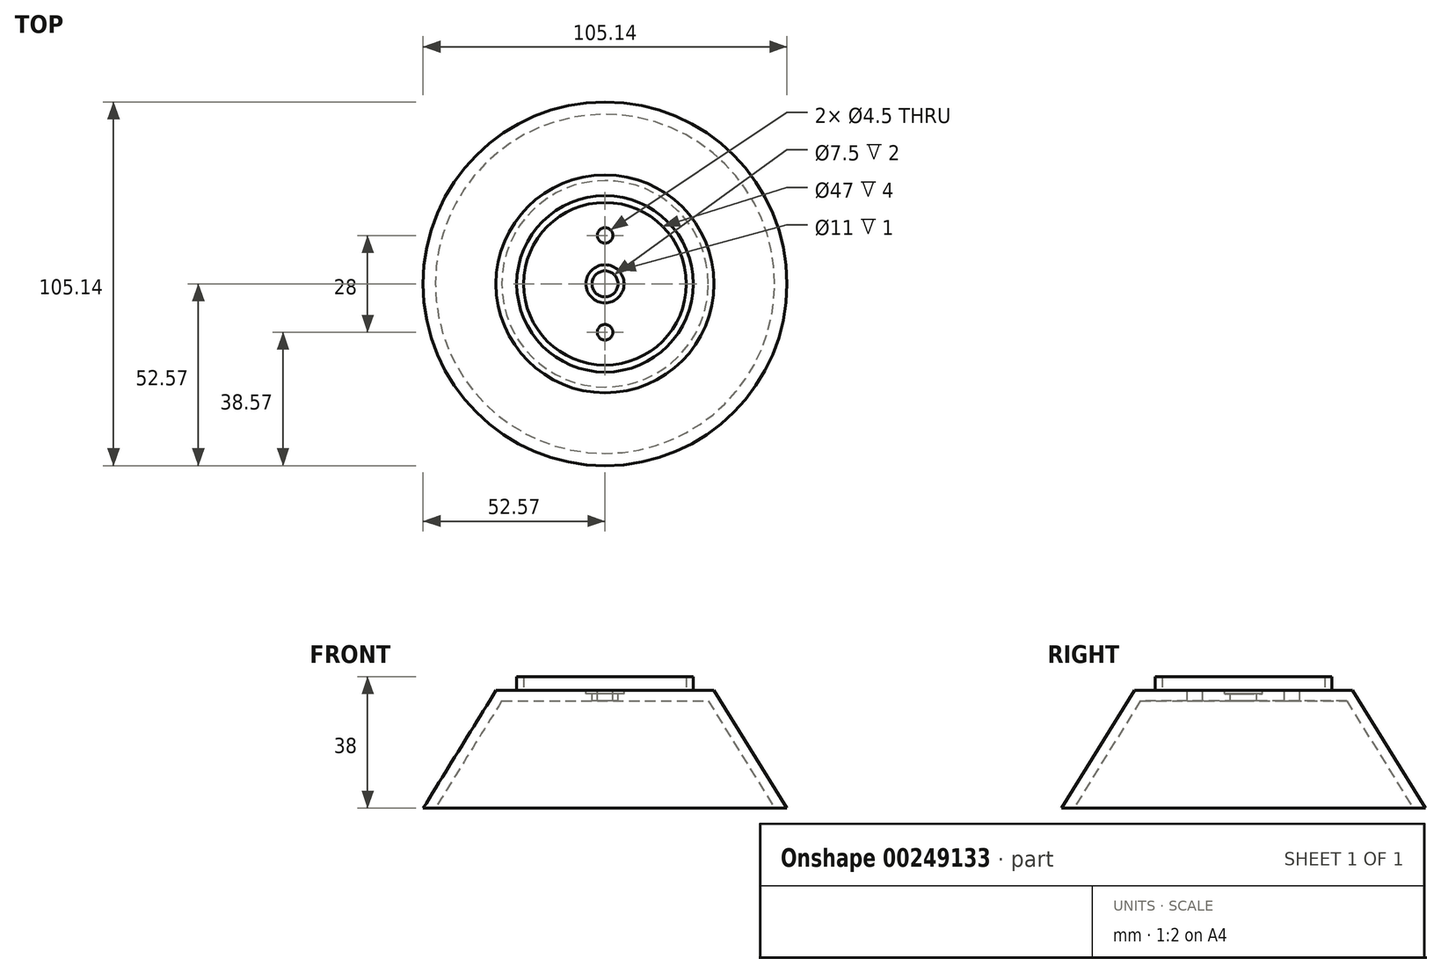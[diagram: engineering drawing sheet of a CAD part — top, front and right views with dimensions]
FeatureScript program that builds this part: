
annotation { "Feature Type Name" : "Feature", "Feature Type Description" : "" }
export const myFeature = defineFeature(function(context is Context, id is Id, definition is map)
    precondition{}
    {
        {
            var Q0;
            Q0=qCreatedBy(makeId("Front.planeOp"),FACE);
            var sketch = newSketch(context, id + "F0", { "sketchPlane" : qUnion([Q0])});
            skLineSegment(sketch, "E0", {"start": v(-23.5, 32.38) * mm, "end": v(-25.5, 32.38) * mm});
            skLineSegment(sketch, "E1", {"start": v(-25.5, 32.38) * mm, "end": v(-25.5, 28.38) * mm});
            skLineSegment(sketch, "E2", {"start": v(-31.5, 28.38) * mm, "end": v(-52.57, -5.62) * mm});
            skLineSegment(sketch, "E3", {"start": v(-49.01, -5.57) * mm, "end": v(-29.83, 25.38) * mm});
            skLineSegment(sketch, "E4", {"start": v(-29.83, 25.38) * mm, "end": v(0, 25.38) * mm});
            skLineSegment(sketch, "E5", {"start": v(0, 25.38) * mm, "end": v(0, 28.38) * mm});
            skLineSegment(sketch, "E6", {"start": v(0, 28.38) * mm, "end": v(-23.5, 28.38) * mm});
            skLineSegment(sketch, "E7", {"start": v(-23.5, 28.38) * mm, "end": v(-23.5, 32.38) * mm});
            skLineSegment(sketch, "E8", {"start": v(-25.5, 28.38) * mm, "end": v(-31.5, 28.38) * mm});
            skLineSegment(sketch, "E9", {"start": v(-52.57, -5.62) * mm, "end": v(-49.01, -5.57) * mm});
            skSolve(sketch);
        }
        {
            var Q0;
            Q0 = qSketchRegion(id + "F0", true);
            var Q1;
            Q1=sQuery(id+"F0.wireOp",EDGE,"E5");
            revolve(context, id + "F1", {"entities" : qUnion([Q0]), "axis" : qUnion([Q1]), "revolveType" : RevolveType.FULL});
        }
        {
            var Q0;
            Q0=makeQuery(id+"F1.opRevolve","SWEPT_FACE",FACE,{"disambiguationData":[OSD([sQuery(id+"F0.wireOp",EDGE,"E6")])]});
            var sketch = newSketch(context, id + "F2", { "sketchPlane" : qUnion([Q0])});
            skCircle(sketch, "E10", {"center": v(0, 0) * mm, "radius": 3.75 * mm});
            skCircle(sketch, "E11", {"center": v(0, -14) * mm, "radius": 2.25 * mm});
            skCircle(sketch, "E12.MirrorC", {"center": v(0, 14) * mm, "radius": 2.25 * mm});
            skSolve(sketch);
        }
        {
            var Q0;
            Q0 = qSketchRegion(id + "F2", true);
            extrude(context, id + "F3", {"entities" : qUnion([Q0]), "operationType" : NewBodyOperationType.REMOVE, "oppositeDirection" : true, "depth" : 25 * mm});
        }
        {
            var Q0;
            Q0=makeQuery(id+"F1.opRevolve","SWEPT_FACE",FACE,{"disambiguationData":[OSD([sQuery(id+"F0.wireOp",EDGE,"E6")])]});
            var sketch = newSketch(context, id + "F4", { "sketchPlane" : qUnion([Q0])});
            skCircle(sketch, "E13", {"center": v(0, 0) * mm, "radius": 5.5 * mm});
            skSolve(sketch);
        }
        {
            var Q0;
            Q0 = qSketchRegion(id + "F4", true);
            extrude(context, id + "F5", {"entities" : qUnion([Q0]), "operationType" : NewBodyOperationType.REMOVE, "oppositeDirection" : true, "depth" : 1 * mm});
        }
    });
